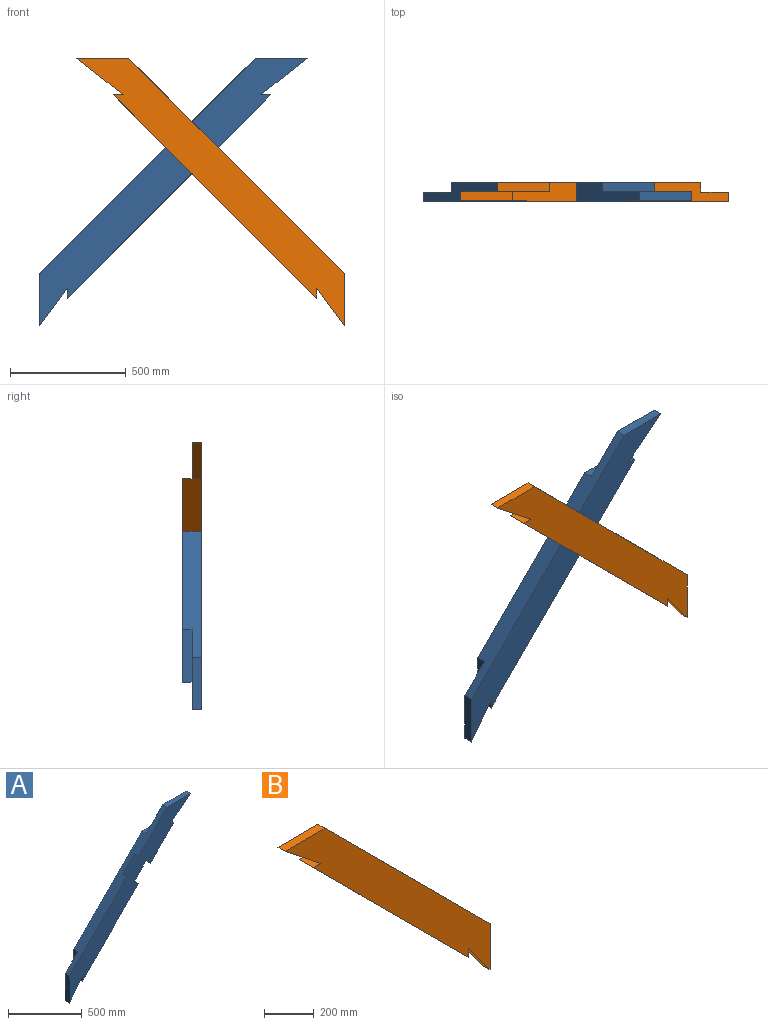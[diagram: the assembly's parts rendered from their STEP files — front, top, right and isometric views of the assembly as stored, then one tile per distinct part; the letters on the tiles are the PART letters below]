
ASSEMBLY  parts=2 mates=1
PART A: 16 faces, bbox 1160x80x1160 mm
  f0: plane 226.27x80mm, normal (-1,0,0), area 10748mm2, adj f1,f3,f4,f11,f14,f15
  f1: plane 880x880mm, normal (0.71,0,-0.71), area 93160.6mm2, adj f0,f2,f4,f5,f7,f9,f12,f15
  f2: plane 226.27x80mm, normal (0,0,1), area 10748mm2, adj f1,f3,f4,f8,f9,f10
  f3: plane 933.73x933.73mm, normal (-0.71,0,0.71), area 83399.8mm2, adj f0,f2,f4,f5,f6,f7,f9,f10
  f4: plane 880x880mm, normal (0,1,0), area 173521.3mm2, adj f0,f1,f2,f3
  f5: plane 226.27x226.27mm, normal (0,-1,0), area 25600mm2, adj f1,f3,f7,f12
  f6: plane 226.27x40mm, normal (0,0,1), area 9051mm2, adj f3,f8,f9,f10
  f7: plane 113.14x113.14mm, normal (-0.71,0,-0.71), area 6400mm2, adj f1,f3,f5,f9
  f8: plane 202.43x160mm, normal (0.62,0,-0.78), area 10321mm2, adj f2,f6,f9,f10
  f9: plane 500x386.86mm, normal (0,-1,0), area 71343mm2, adj f1,f2,f3,f6,f7,f8
  f10: plane 386.27x160mm, normal (0,1,0), area 32809.8mm2, adj f2,f3,f6,f8
  f11: plane 346.27x120mm, normal (0,1,0), area 24607.3mm2, adj f0,f3,f13,f14
  f12: plane 113.14x113.14mm, normal (0.71,0,0.71), area 6400mm2, adj f1,f3,f5,f15
  f13: plane 226.27x40mm, normal (-1,0,0), area 9051mm2, adj f3,f11,f14,f15
  f14: plane 162.43x120mm, normal (0.8,0,-0.59), area 8077.9mm2, adj f0,f11,f13,f15
  f15: plane 773.14x660mm, normal (0,-1,0), area 133995.4mm2, adj f0,f1,f3,f12,f13,f14
PART B: 16 faces, bbox 1160x80x1160 mm
  f0: plane 226.27x226.27mm, normal (0,1,0), area 25600mm2, adj f5,f9,f12,f14
  f1: plane 386.27x160mm, normal (0,1,0), area 32809.8mm2, adj f5,f6,f7,f8
  f2: plane 346.27x120mm, normal (0,1,0), area 24607.3mm2, adj f3,f4,f5,f10
  f3: plane 162.43x120mm, normal (-0.8,0,-0.59), area 8077.9mm2, adj f2,f4,f10,f11
  f4: plane 226.27x40mm, normal (1,0,0), area 9051mm2, adj f2,f3,f5,f11
  f5: plane 933.73x933.73mm, normal (0.71,0,0.71), area 83399.8mm2, adj f0,f1,f2,f4,f6,f8,f10,f11
  f6: plane 226.27x40mm, normal (0,0,1), area 9051mm2, adj f1,f5,f7,f11
  f7: plane 202.43x160mm, normal (-0.62,0,-0.78), area 10321mm2, adj f1,f6,f8,f11
  f8: plane 226.27x80mm, normal (0,0,1), area 10748mm2, adj f1,f5,f7,f9,f11,f13
  f9: plane 880x880mm, normal (-0.71,0,-0.71), area 93160.6mm2, adj f0,f8,f10,f11,f12,f13,f14,f15
  f10: plane 226.27x80mm, normal (1,0,0), area 10748mm2, adj f2,f3,f5,f9,f11,f15
  f11: plane 1160x1160mm, normal (0,-1,0), area 230938.3mm2, adj f3,f4,f5,f6,f7,f8,f9,f10
  f12: plane 113.14x113.14mm, normal (0.71,0,-0.71), area 6400mm2, adj f0,f5,f9,f13
  f13: plane 340x226.86mm, normal (0,1,0), area 38533.2mm2, adj f5,f8,f9,f12
  f14: plane 113.14x113.14mm, normal (-0.71,0,0.71), area 6400mm2, adj f0,f5,f9,f15
  f15: plane 653.14x540mm, normal (0,1,0), area 109388.1mm2, adj f5,f9,f10,f14
PLACE A t=(-520.75,282.81,-1114.08)mm
PLACE B t=(-520.75,282.81,-1114.08)mm
MATE fastened A.f5 <-> B.f0  axis (0,-1,0) through (-520.75,282.81,899.06)mm
